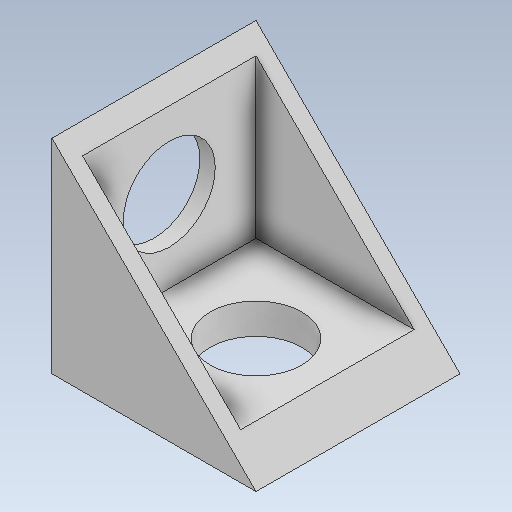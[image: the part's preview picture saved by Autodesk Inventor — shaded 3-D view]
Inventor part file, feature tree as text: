
AUTODESK INVENTOR PART (.ipt)
format: ipt  version: 2023 (Build 270158000, 158)  size: 124,928 bytes
history: native  units: in
note: dims shown in document units (in); Inventor stores cm internally (conversion verified against a paired STEP export)
features: sketch x5, other x3
ambient origin geometry x8: Origin, YZ Plane, XZ Plane, XY Plane, X Axis, Y Axis, Z Axis, Center Point
bodies: Solid1 (feature_tree)
feature tree (8):
  other  "CH-1-01-Cornerbracket.ipt"
  other  "Solid1::CH-1-01-Cornerbracket.ipt"
  other  "TaggingFeature1"
  sketch  "Sketch1"  dims[d0=0.3937in]
  sketch  "Sketch2"
  sketch  "Sketch6"
  sketch  "Sketch7"
  sketch  "Sketch8"
